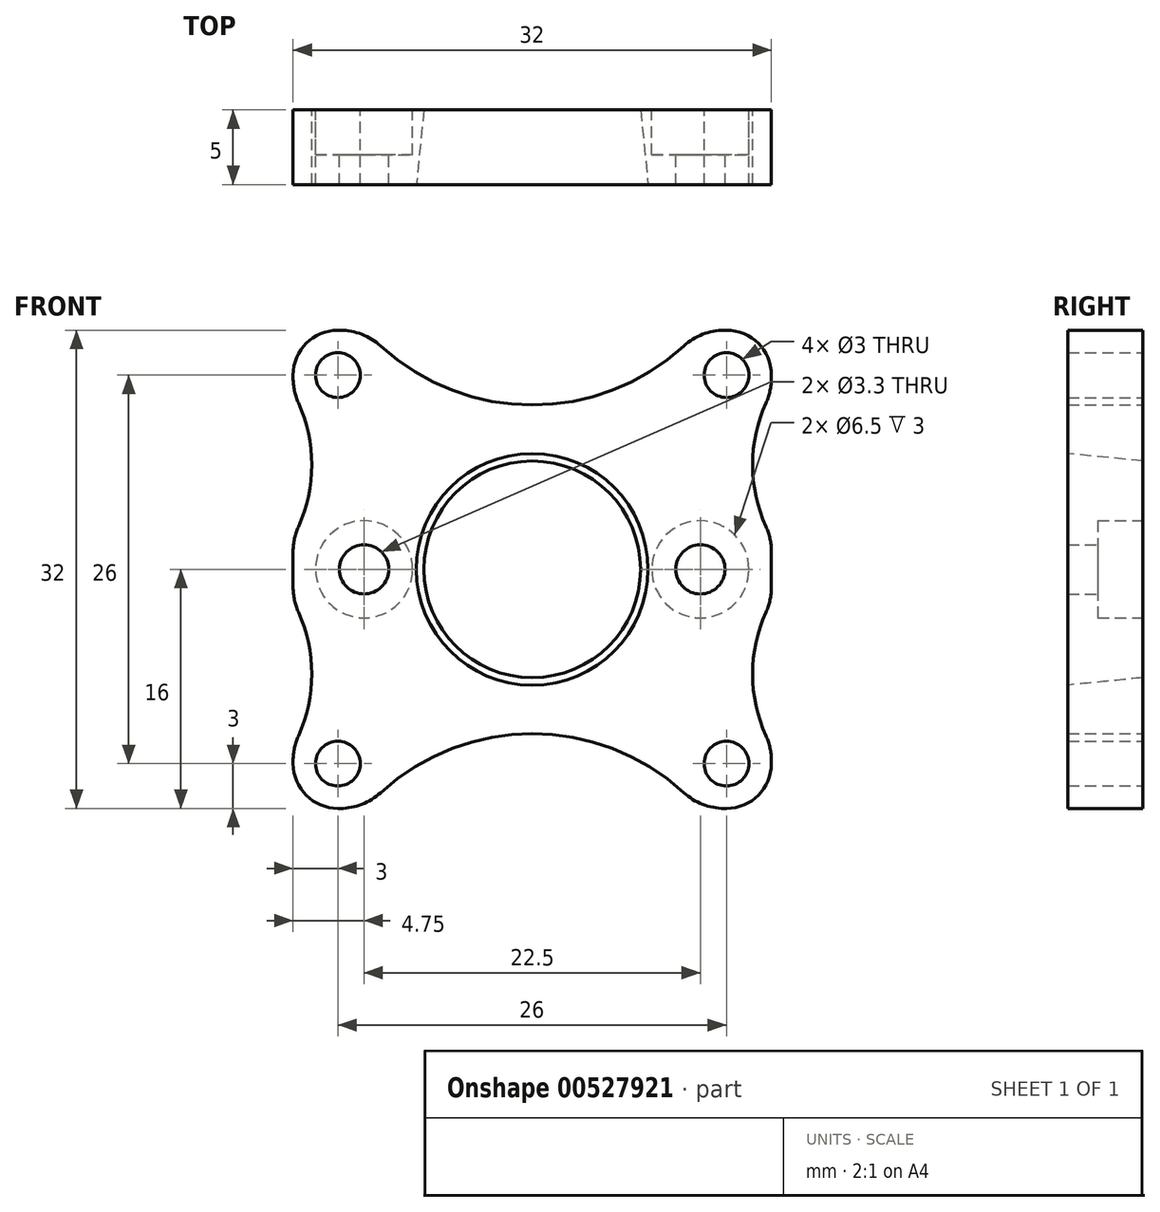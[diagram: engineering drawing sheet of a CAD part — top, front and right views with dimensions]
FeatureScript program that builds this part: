
annotation { "Feature Type Name" : "Feature", "Feature Type Description" : "" }
export const myFeature = defineFeature(function(context is Context, id is Id, definition is map)
    precondition{}
    {
        {
            var Q0;
            Q0=qCreatedBy(makeId("Front.planeOp"),FACE);
            var sketch = newSketch(context, id + "F0", { "sketchPlane" : qUnion([Q0])});
            skLineSegment(sketch, "E0.bottom", {"start": v(16, -16) * mm, "end": v(-16, -16) * mm});
            skLineSegment(sketch, "E0.top", {"start": v(16, 16) * mm, "end": v(-16, 16) * mm});
            skLineSegment(sketch, "E0.left", {"start": v(16, -16) * mm, "end": v(16, 16) * mm});
            skLineSegment(sketch, "E0.right", {"start": v(-16, -16) * mm, "end": v(-16, 16) * mm});
            skPoint(sketch, "E0.middle", {"position": v(0, 0) * mm});
            skCircle(sketch, "E1", {"center": v(-13, 13) * mm, "radius": 1.5 * mm});
            skCircle(sketch, "E2.MirrorC", {"center": v(13, 13) * mm, "radius": 1.5 * mm});
            skCircle(sketch, "E3.MirrorC", {"center": v(-13, -13) * mm, "radius": 1.5 * mm});
            skCircle(sketch, "E4.MirrorC", {"center": v(13, -13) * mm, "radius": 1.5 * mm});
            skCircle(sketch, "E5", {"center": v(0, 0) * mm, "radius": 7.25 * mm});
            skPoint(sketch, "E6", {"position": v(11.25, 0) * mm});
            skPoint(sketch, "E7", {"position": v(-11.25, 0) * mm});
            skPoint(sketch, "E8.centerSnap0", {"position": v(0, 16) * mm});
            skArc(sketch, "E9", {"start": v(11.18, 16) * mm, "mid": v(0, 11) * mm, "end": v(-11.18, 16) * mm});
            skArc(sketch, "E10.MirrorCS", {"start": v(11.18, -16) * mm, "mid": v(0, -11) * mm, "end": v(-11.18, -16) * mm});
            skLineSegment(sketch, "E11", {"start": v(-16, 7) * mm, "end": v(16, 7) * mm, "construction": true});
            skLineSegment(sketch, "E12", {"start": v(-16, -8) * mm, "end": v(16, -8) * mm, "construction": true});
            skArc(sketch, "E13", {"start": v(16, 2.15) * mm, "mid": v(14.74, 7) * mm, "end": v(16, 11.85) * mm});
            skArc(sketch, "E14.MirrorCS", {"start": v(-16, 2.15) * mm, "mid": v(-14.74, 7) * mm, "end": v(-16, 11.85) * mm});
            skArc(sketch, "E15.MirrorCS", {"start": v(16, -2.15) * mm, "mid": v(14.74, -7) * mm, "end": v(16, -11.85) * mm});
            skArc(sketch, "E16.MirrorCS", {"start": v(-16, -2.15) * mm, "mid": v(-14.74, -7) * mm, "end": v(-16, -11.85) * mm});
            skSolve(sketch);
        }
        {
            var Q0;
            {var subQ0=sQuery(id+"F0.wireOp",EDGE,"E0.right");Q0=makeQuery(id+"F0.imprint","IMPRINT",FACE,{"disambiguationData":[TD([[makeQuery(id+"F0.imprint","IMPRINT",EDGE,{"derivedFrom":subQ0}),-1.0]])]});}
            extrude(context, id + "F1", {"entities" : qUnion([Q0]), "depth" : 5 * mm, "offsetDistance" : 25 * mm});
        }
        {
            var Q0;
            Q0=makeQuery(id+"F1.opExtrude","SWEPT_EDGE",EDGE,{"disambiguationData":[OSD([sQuery(id+"F0.wireOp",EDGE,"E0.top"),sQuery(id+"F0.wireOp",EDGE,"E0.right")])]});
            var Q1;
            Q1=makeQuery(id+"F1.opExtrude","SWEPT_EDGE",EDGE,{"disambiguationData":[OSD([sQuery(id+"F0.wireOp",EDGE,"E0.top"),sQuery(id+"F0.wireOp",EDGE,"E0.left")])]});
            var Q2;
            Q2=makeQuery(id+"F1.opExtrude","SWEPT_EDGE",EDGE,{"disambiguationData":[OSD([sQuery(id+"F0.wireOp",EDGE,"E0.bottom"),sQuery(id+"F0.wireOp",EDGE,"E0.left")])]});
            var Q3;
            Q3=makeQuery(id+"F1.opExtrude","SWEPT_EDGE",EDGE,{"disambiguationData":[OSD([sQuery(id+"F0.wireOp",EDGE,"E0.bottom"),sQuery(id+"F0.wireOp",EDGE,"E0.right")])]});
            fillet(context, id + "F2", {"entities" : qUnion([Q0, Q1, Q2, Q3]), "radius" : 3 * mm, "tangentPropagation" : true, "allowEdgeOverflow" : false});
        }
        {
            var Q0;
            Q0=makeQuery(id+"F1.opExtrude","CAP_EDGE",EDGE,{"disambiguationData":[OSD([sQuery(id+"F0.wireOp",EDGE,"E5")])],"isStart":false});
            chamfer(context, id + "F3", {"entities" : qUnion([Q0]), "chamferType" : ChamferType.TWO_OFFSETS, "width1" : 0.5 * mm, "oppositeDirection" : true, "width2" : 5 * mm, "tangentPropagation" : true});
        }
        {
            var Q0;
            Q0=sQuery(id+"F0.wireOp",VERTEX,"E6");
            var Q1;
            Q1=sQuery(id+"F0.wireOp",VERTEX,"E7");
            var Q2;
            Q2=makeQuery(id+"F1.opExtrude","SWEPT_BODY",BODY,{"disambiguationData":[OSD([sQuery(id+"F0.wireOp",EDGE,"E0.bottom"),sQuery(id+"F0.wireOp",EDGE,"E0.top"),sQuery(id+"F0.wireOp",EDGE,"E0.left"),sQuery(id+"F0.wireOp",EDGE,"E0.right"),sQuery(id+"F0.wireOp",EDGE,"E1"),sQuery(id+"F0.wireOp",EDGE,"E2.MirrorC"),sQuery(id+"F0.wireOp",EDGE,"E3.MirrorC"),sQuery(id+"F0.wireOp",EDGE,"E4.MirrorC"),sQuery(id+"F0.wireOp",EDGE,"E5")])]});
            hole(context, id + "F4", {"style" : HoleStyle.C_BORE, "endStyle" : HoleEndStyle.THROUGH, "oppositeDirection" : true, "standardTappedOrClearance" : lookupTablePath({ "standard" : "ISO", "fit" : "Normal", "size" : "M3", "type" : "Clearance" }), "standardBlindInLast" : lookupTablePath({ "fit" : "Standard", "standard" : "ISO", "size" : "M3", "type" : "Clearance" }), "holeDiameter" : 3.3 * mm, "cBoreDiameter" : 6.5 * mm, "cBoreDepth" : 3 * mm, "isTappedThrough" : true, "tappedDepth" : 12 * mm, "tapClearance" : 3, "locations" : qUnion([Q0, Q1]), "scope" : qUnion([Q2])});
        }
        {
            var Q0;
            {var subQ0=sQuery(id+"F0.wireOp",EDGE,"E16.MirrorCS");var subQ1=sQuery(id+"F0.wireOp",EDGE,"E0.right");Q0=makeQuery(id+"F1.opExtrude","SWEPT_EDGE",EDGE,{"disambiguationData":[OSD([subQ1,subQ0]),TDD([makeQuery(id+"F0.imprint","INTERSECT",VERTEX,{"disambiguationData":[OD(0.0)],"derivedFrom":[subQ1,subQ0]})])]});}
            var Q1;
            {var subQ0=sQuery(id+"F0.wireOp",EDGE,"E14.MirrorCS");var subQ1=sQuery(id+"F0.wireOp",EDGE,"E0.right");Q1=makeQuery(id+"F1.opExtrude","SWEPT_EDGE",EDGE,{"disambiguationData":[OSD([subQ1,subQ0]),TDD([makeQuery(id+"F0.imprint","INTERSECT",VERTEX,{"disambiguationData":[OD(0.0)],"derivedFrom":[subQ1,subQ0]})])]});}
            var Q2;
            {var subQ0=sQuery(id+"F0.wireOp",EDGE,"E14.MirrorCS");var subQ1=sQuery(id+"F0.wireOp",EDGE,"E0.right");Q2=makeQuery(id+"F1.opExtrude","SWEPT_EDGE",EDGE,{"disambiguationData":[OSD([subQ1,subQ0]),TDD([makeQuery(id+"F0.imprint","INTERSECT",VERTEX,{"disambiguationData":[OD(1.0)],"derivedFrom":[subQ1,subQ0]})])]});}
            var Q3;
            {var subQ0=sQuery(id+"F0.wireOp",EDGE,"E0.right");var subQ1=sQuery(id+"F0.wireOp",EDGE,"E0.top");Q3=makeQuery(id+"F2.opFillet","BLEND_EDGE",EDGE,{"blendedFrom":[makeQuery(id+"F1.opExtrude","SWEPT_EDGE",EDGE,{"disambiguationData":[OSD([subQ1,subQ0])]}),makeQuery(id+"F1.opExtrude","SWEPT_FACE",FACE,{"disambiguationData":[OSD([subQ0]),TDD([makeQuery(id+"F0.imprint","IMPRINT",EDGE,{"disambiguationData":[TD([[makeQuery(id+"F0.imprint","INTERSECT",VERTEX,{"derivedFrom":[subQ1,subQ0]}),1.0]])],"derivedFrom":subQ0})])]})],"blendedInto":[makeQuery(id+"F1.opExtrude","SWEPT_FACE",FACE,{"disambiguationData":[OSD([subQ0]),TDD([makeQuery(id+"F0.imprint","IMPRINT",EDGE,{"disambiguationData":[TD([[makeQuery(id+"F0.imprint","INTERSECT",VERTEX,{"derivedFrom":[subQ1,subQ0]}),1.0]])],"derivedFrom":subQ0})])]})]});}
            var Q4;
            {var subQ0=sQuery(id+"F0.wireOp",EDGE,"E9");var subQ1=sQuery(id+"F0.wireOp",EDGE,"E0.top");Q4=makeQuery(id+"F1.opExtrude","SWEPT_EDGE",EDGE,{"disambiguationData":[OSD([subQ1,subQ0]),TDD([makeQuery(id+"F0.imprint","INTERSECT",VERTEX,{"disambiguationData":[OD(1.0)],"derivedFrom":[subQ1,subQ0]})])]});}
            var Q5;
            {var subQ0=sQuery(id+"F0.wireOp",EDGE,"E9");var subQ1=sQuery(id+"F0.wireOp",EDGE,"E0.top");Q5=makeQuery(id+"F1.opExtrude","SWEPT_EDGE",EDGE,{"disambiguationData":[OSD([subQ1,subQ0]),TDD([makeQuery(id+"F0.imprint","INTERSECT",VERTEX,{"disambiguationData":[OD(0.0)],"derivedFrom":[subQ1,subQ0]})])]});}
            var Q6;
            {var subQ0=sQuery(id+"F0.wireOp",EDGE,"E13");var subQ1=sQuery(id+"F0.wireOp",EDGE,"E0.left");Q6=makeQuery(id+"F1.opExtrude","SWEPT_EDGE",EDGE,{"disambiguationData":[OSD([subQ1,subQ0]),TDD([makeQuery(id+"F0.imprint","INTERSECT",VERTEX,{"disambiguationData":[OD(1.0)],"derivedFrom":[subQ1,subQ0]})])]});}
            var Q7;
            {var subQ0=sQuery(id+"F0.wireOp",EDGE,"E13");var subQ1=sQuery(id+"F0.wireOp",EDGE,"E0.left");Q7=makeQuery(id+"F1.opExtrude","SWEPT_EDGE",EDGE,{"disambiguationData":[OSD([subQ1,subQ0]),TDD([makeQuery(id+"F0.imprint","INTERSECT",VERTEX,{"disambiguationData":[OD(0.0)],"derivedFrom":[subQ1,subQ0]})])]});}
            var Q8;
            {var subQ0=sQuery(id+"F0.wireOp",EDGE,"E15.MirrorCS");var subQ1=sQuery(id+"F0.wireOp",EDGE,"E0.left");Q8=makeQuery(id+"F1.opExtrude","SWEPT_EDGE",EDGE,{"disambiguationData":[OSD([subQ1,subQ0]),TDD([makeQuery(id+"F0.imprint","INTERSECT",VERTEX,{"disambiguationData":[OD(0.0)],"derivedFrom":[subQ1,subQ0]})])]});}
            var Q9;
            {var subQ0=sQuery(id+"F0.wireOp",EDGE,"E15.MirrorCS");var subQ1=sQuery(id+"F0.wireOp",EDGE,"E0.left");Q9=makeQuery(id+"F1.opExtrude","SWEPT_EDGE",EDGE,{"disambiguationData":[OSD([subQ1,subQ0]),TDD([makeQuery(id+"F0.imprint","INTERSECT",VERTEX,{"disambiguationData":[OD(1.0)],"derivedFrom":[subQ1,subQ0]})])]});}
            var Q10;
            {var subQ0=sQuery(id+"F0.wireOp",EDGE,"E10.MirrorCS");var subQ1=sQuery(id+"F0.wireOp",EDGE,"E0.bottom");Q10=makeQuery(id+"F1.opExtrude","SWEPT_EDGE",EDGE,{"disambiguationData":[OSD([subQ1,subQ0]),TDD([makeQuery(id+"F0.imprint","INTERSECT",VERTEX,{"disambiguationData":[OD(0.0)],"derivedFrom":[subQ1,subQ0]})])]});}
            var Q11;
            {var subQ0=sQuery(id+"F0.wireOp",EDGE,"E10.MirrorCS");var subQ1=sQuery(id+"F0.wireOp",EDGE,"E0.bottom");Q11=makeQuery(id+"F1.opExtrude","SWEPT_EDGE",EDGE,{"disambiguationData":[OSD([subQ1,subQ0]),TDD([makeQuery(id+"F0.imprint","INTERSECT",VERTEX,{"disambiguationData":[OD(1.0)],"derivedFrom":[subQ1,subQ0]})])]});}
            var Q12;
            {var subQ0=sQuery(id+"F0.wireOp",EDGE,"E16.MirrorCS");var subQ1=sQuery(id+"F0.wireOp",EDGE,"E0.right");Q12=makeQuery(id+"F1.opExtrude","SWEPT_EDGE",EDGE,{"disambiguationData":[OSD([subQ1,subQ0]),TDD([makeQuery(id+"F0.imprint","INTERSECT",VERTEX,{"disambiguationData":[OD(1.0)],"derivedFrom":[subQ1,subQ0]})])]});}
            fillet(context, id + "F5", {"entities" : qUnion([Q0, Q1, Q2, Q3, Q4, Q5, Q6, Q7, Q8, Q9, Q10, Q11, Q12]), "radius" : 4 * mm, "tangentPropagation" : true, "allowEdgeOverflow" : false});
        }
    });
